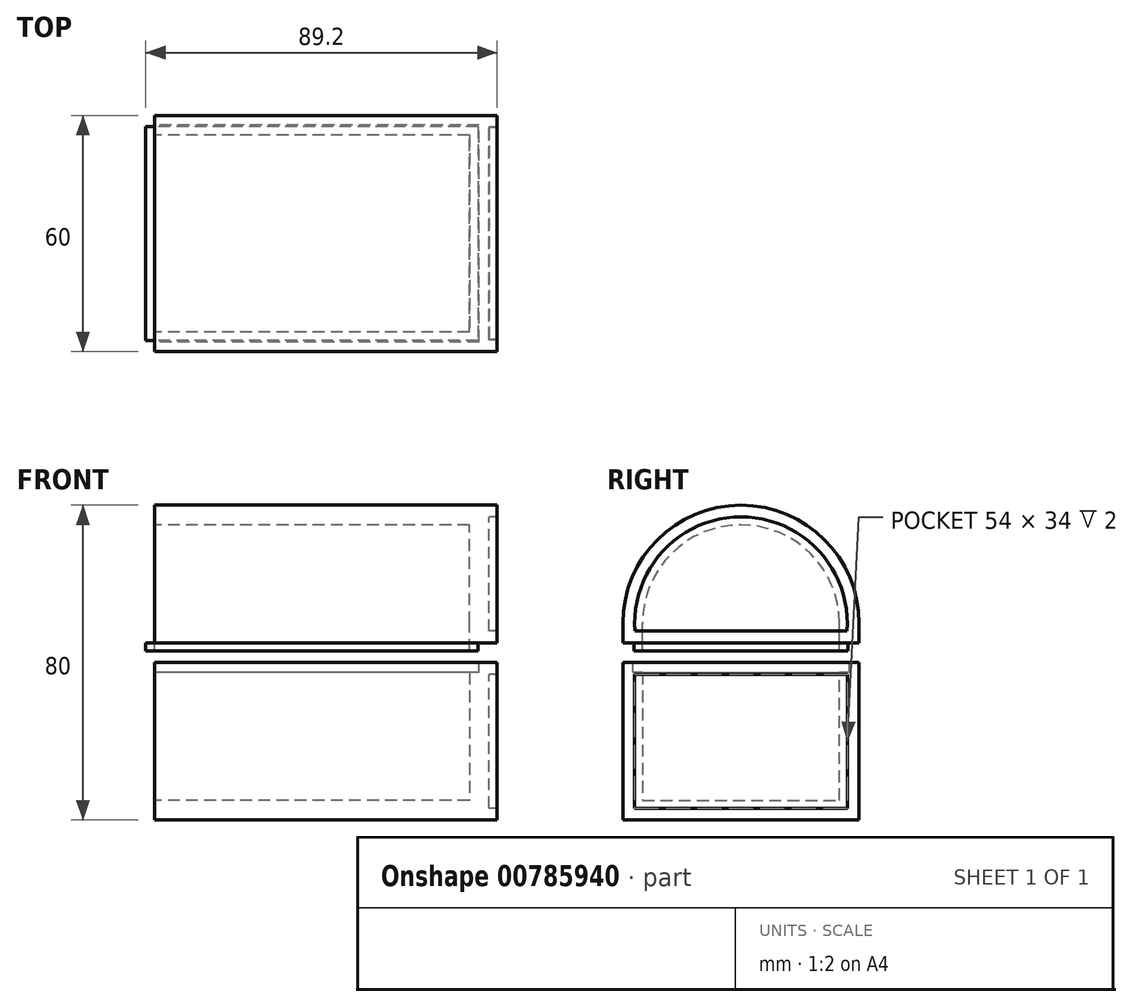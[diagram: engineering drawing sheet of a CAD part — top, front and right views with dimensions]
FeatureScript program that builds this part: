
annotation { "Feature Type Name" : "Feature", "Feature Type Description" : "" }
export const myFeature = defineFeature(function(context is Context, id is Id, definition is map)
    precondition{}
    {
        {
            var Q0;
            Q0=qCreatedBy(makeId("Right.planeOp"),FACE);
            var sketch = newSketch(context, id + "F0", { "sketchPlane" : qUnion([Q0])});
            skLineSegment(sketch, "E0.left", {"start": v(-30, 0) * mm, "end": v(-30, -40) * mm});
            skLineSegment(sketch, "E1.bottom", {"start": v(-30, -40) * mm, "end": v(30, -40) * mm});
            skLineSegment(sketch, "E2.left", {"start": v(30, -40) * mm, "end": v(30, 0) * mm});
            skLineSegment(sketch, "E3.0", {"start": v(25, -35) * mm, "end": v(25, 0) * mm});
            skLineSegment(sketch, "E3.1", {"start": v(-25, -35) * mm, "end": v(25, -35) * mm});
            skLineSegment(sketch, "E3.2", {"start": v(-25, 0) * mm, "end": v(-25, -35) * mm});
            skLineSegment(sketch, "E4", {"start": v(-25, 0) * mm, "end": v(-30, 0) * mm});
            skLineSegment(sketch, "E5", {"start": v(30, 0) * mm, "end": v(25, 0) * mm});
            skSolve(sketch);
        }
        {
            var Q0;
            Q0 = qSketchRegion(id + "F0", true);
            extrude(context, id + "F1", {"entities" : qUnion([Q0]), "endBound" : BoundingType.SYMMETRIC, "depth" : 80 * mm, "offsetDistance" : 25 * mm});
        }
        {
            var Q0;
            Q0=makeQuery(id+"F1.opExtrude","CAP_FACE",FACE,{"disambiguationData":[OSD([sQuery(id+"F0.wireOp",EDGE,"E0.left"),sQuery(id+"F0.wireOp",EDGE,"E1.bottom"),sQuery(id+"F0.wireOp",EDGE,"E2.left"),sQuery(id+"F0.wireOp",EDGE,"E3.0"),sQuery(id+"F0.wireOp",EDGE,"E3.1"),sQuery(id+"F0.wireOp",EDGE,"E3.2"),sQuery(id+"F0.wireOp",EDGE,"E4"),sQuery(id+"F0.wireOp",EDGE,"E5")])],"isStart":false});
            var sketch = newSketch(context, id + "F2", { "sketchPlane" : qUnion([Q0])});
            skLineSegment(sketch, "E6.bottom", {"start": v(-30, 0) * mm, "end": v(30, 0) * mm});
            skLineSegment(sketch, "E6.top", {"start": v(-30, -40) * mm, "end": v(30, -40) * mm});
            skLineSegment(sketch, "E6.left", {"start": v(-30, 0) * mm, "end": v(-30, -40) * mm});
            skLineSegment(sketch, "E6.right", {"start": v(30, 0) * mm, "end": v(30, -40) * mm});
            skSolve(sketch);
        }
        {
            var Q0;
            Q0 = qSketchRegion(id + "F2", true);
            extrude(context, id + "F3", {"entities" : qUnion([Q0]), "operationType" : NewBodyOperationType.ADD, "depth" : 5 * mm, "offsetDistance" : 25 * mm});
        }
        {
            var Q0;
            Q0=makeQuery(id+"F6EYYDIKWfOxyM3_1.boolean.opBoolean","MERGE",FACE,{"derivedFrom":[makeQuery(id+"F3.boolean.opBoolean","MERGE",FACE,{"derivedFrom":[makeQuery(id+"F1.opExtrude","SWEPT_FACE",FACE,{"disambiguationData":[OSD([sQuery(id+"F0.wireOp",EDGE,"E4")])]}),makeQuery(id+"F1.opExtrude","SWEPT_FACE",FACE,{"disambiguationData":[OSD([sQuery(id+"F0.wireOp",EDGE,"E5")])]}),makeQuery(id+"F3.opExtrude","SWEPT_FACE",FACE,{"disambiguationData":[OSD([sQuery(id+"F2.wireOp",EDGE,"E6.bottom")])]})]}),makeQuery(id+"F6EYYDIKWfOxyM3_1.opExtrude","SWEPT_FACE",FACE,{"disambiguationData":[OSD([sQuery(id+"FPHd44v9Huq2bwW_1.wireOp",EDGE,"AvJGf5aJ-Tb4b-4m7N-2CrS-YhxYk3OROw7q.bottom")])]})]});
            var sketch = newSketch(context, id + "F4", { "sketchPlane" : qUnion([Q0])});
            skLineSegment(sketch, "E7.0", {"start": v(40, -25) * mm, "end": v(40, 25) * mm});
            skLineSegment(sketch, "E8.0", {"start": v(40, -25) * mm, "end": v(-40, -25) * mm});
            skLineSegment(sketch, "E9.0", {"start": v(40, 25) * mm, "end": v(-40, 25) * mm});
            skLineSegment(sketch, "E10.0", {"start": v(-40, 25) * mm, "end": v(-40, -25) * mm});
            skLineSegment(sketch, "E11.0", {"start": v(42.5, -27.5) * mm, "end": v(42.5, 27.5) * mm});
            skLineSegment(sketch, "E11.1", {"start": v(42.5, -27.5) * mm, "end": v(-42.5, -27.5) * mm});
            skLineSegment(sketch, "E11.2", {"start": v(-42.5, 27.5) * mm, "end": v(-42.5, -27.5) * mm});
            skLineSegment(sketch, "E11.3", {"start": v(42.5, 27.5) * mm, "end": v(-42.5, 27.5) * mm});
            skSolve(sketch);
        }
        {
            var Q0;
            Q0 = qSketchRegion(id + "F4", true);
            extrude(context, id + "F5", {"entities" : qUnion([Q0]), "operationType" : NewBodyOperationType.REMOVE, "oppositeDirection" : true, "depth" : 2.5 * mm, "offsetDistance" : 25 * mm});
        }
        {
            var Q0;
            Q0=makeQuery(id+"F6EYYDIKWfOxyM3_1.boolean.opBoolean","MERGE",FACE,{"derivedFrom":[makeQuery(id+"F3.boolean.opBoolean","MERGE",FACE,{"derivedFrom":[makeQuery(id+"F1.opExtrude","SWEPT_FACE",FACE,{"disambiguationData":[OSD([sQuery(id+"F0.wireOp",EDGE,"E4")])]}),makeQuery(id+"F1.opExtrude","SWEPT_FACE",FACE,{"disambiguationData":[OSD([sQuery(id+"F0.wireOp",EDGE,"E5")])]}),makeQuery(id+"F3.opExtrude","SWEPT_FACE",FACE,{"disambiguationData":[OSD([sQuery(id+"F2.wireOp",EDGE,"E6.bottom")])]})]}),makeQuery(id+"F6EYYDIKWfOxyM3_1.opExtrude","SWEPT_FACE",FACE,{"disambiguationData":[OSD([sQuery(id+"FPHd44v9Huq2bwW_1.wireOp",EDGE,"AvJGf5aJ-Tb4b-4m7N-2CrS-YhxYk3OROw7q.bottom")])]})]});
            cPlane(context, id + "F6", {"entities" : qUnion([Q0]), "cplaneType" : CPlaneType.OFFSET, "offset" : 5 * mm, "width" : 150 * mm, "height" : 150 * mm});
        }
        {
            var Q0;
            Q0=qCreatedBy(makeId("Right.planeOp"),FACE);
            var sketch = newSketch(context, id + "F7", { "sketchPlane" : qUnion([Q0])});
            skLineSegment(sketch, "E12", {"start": v(-30, 5) * mm, "end": v(-30, 10) * mm});
            skLineSegment(sketch, "E13", {"start": v(30, 5) * mm, "end": v(30, 10) * mm});
            skArc(sketch, "E14", {"start": v(30, 10) * mm, "mid": v(0, 40) * mm, "end": v(-30, 10) * mm});
            skLineSegment(sketch, "E15.0", {"start": v(25, 5) * mm, "end": v(25, 10) * mm});
            skArc(sketch, "E15.1", {"start": v(25, 10) * mm, "mid": v(0, 35) * mm, "end": v(-25, 10) * mm});
            skLineSegment(sketch, "E15.2", {"start": v(-25, 5) * mm, "end": v(-25, 10) * mm});
            skLineSegment(sketch, "E16", {"start": v(-30, 5) * mm, "end": v(-25, 5) * mm});
            skLineSegment(sketch, "E17", {"start": v(30, 5) * mm, "end": v(25, 5) * mm});
            skSolve(sketch);
        }
        {
            var Q0;
            Q0 = qSketchRegion(id + "F7", true);
            extrude(context, id + "F8", {"entities" : qUnion([Q0]), "endBound" : BoundingType.SYMMETRIC, "depth" : 80 * mm, "offsetDistance" : 25 * mm});
        }
        {
            var Q0;
            Q0=makeQuery(id+"F8.opExtrude","CAP_FACE",FACE,{"disambiguationData":[OSD([sQuery(id+"F7.wireOp",EDGE,"E12"),sQuery(id+"F7.wireOp",EDGE,"E13"),sQuery(id+"F7.wireOp",EDGE,"E14"),sQuery(id+"F7.wireOp",EDGE,"E15.0"),sQuery(id+"F7.wireOp",EDGE,"E15.1"),sQuery(id+"F7.wireOp",EDGE,"E15.2"),sQuery(id+"F7.wireOp",EDGE,"E16"),sQuery(id+"F7.wireOp",EDGE,"E17")])],"isStart":false});
            var sketch = newSketch(context, id + "F9", { "sketchPlane" : qUnion([Q0])});
            skArc(sketch, "E18.0", {"start": v(30, 10) * mm, "mid": v(0, 40) * mm, "end": v(-30, 10) * mm});
            skLineSegment(sketch, "E19.0", {"start": v(-30, 5) * mm, "end": v(-30, 10) * mm});
            skLineSegment(sketch, "E20.0", {"start": v(30, 5) * mm, "end": v(30, 10) * mm});
            skLineSegment(sketch, "E21", {"start": v(-30, 5) * mm, "end": v(30, 5) * mm});
            skSolve(sketch);
        }
        {
            var Q0;
            Q0 = qSketchRegion(id + "F9", true);
            extrude(context, id + "F10", {"entities" : qUnion([Q0]), "operationType" : NewBodyOperationType.ADD, "depth" : 5 * mm, "offsetDistance" : 25 * mm});
        }
        {
            var Q0;
            {var subQ0=sQuery(id+"F9.wireOp",EDGE,"E21");Q0=makeQuery(id+"FFZjNm2Aa1Fzhp1_2.1.F10.boolean.opBoolean","MERGE",FACE,{"derivedFrom":[makeQuery(id+"F10.boolean.opBoolean","MERGE",FACE,{"derivedFrom":[makeQuery(id+"F8.opExtrude","SWEPT_FACE",FACE,{"disambiguationData":[OSD([sQuery(id+"F7.wireOp",EDGE,"E16")])]}),makeQuery(id+"F8.opExtrude","SWEPT_FACE",FACE,{"disambiguationData":[OSD([sQuery(id+"F7.wireOp",EDGE,"E17")])]}),makeQuery(id+"F10.opExtrude","SWEPT_FACE",FACE,{"disambiguationData":[OSD([subQ0])]})]}),makeQuery(id+"FFZjNm2Aa1Fzhp1_2.1.F10.opExtrude","SWEPT_FACE",FACE,{"disambiguationData":[OSD([subQ0])]})]});}
            var sketch = newSketch(context, id + "F11", { "sketchPlane" : qUnion([Q0])});
            skLineSegment(sketch, "E22.0", {"start": v(40, 25) * mm, "end": v(-40, 25) * mm});
            skLineSegment(sketch, "E23.0", {"start": v(-40, -25) * mm, "end": v(-40, 25) * mm});
            skLineSegment(sketch, "E24.0", {"start": v(40, -25) * mm, "end": v(-40, -25) * mm});
            skLineSegment(sketch, "E25.0", {"start": v(40, -25) * mm, "end": v(40, 25) * mm});
            skLineSegment(sketch, "E26.0", {"start": v(42.2, 27.2) * mm, "end": v(-42.2, 27.2) * mm});
            skLineSegment(sketch, "E26.1", {"start": v(42.2, -27.2) * mm, "end": v(42.2, 27.2) * mm});
            skLineSegment(sketch, "E26.2", {"start": v(42.2, -27.2) * mm, "end": v(-42.2, -27.2) * mm});
            skLineSegment(sketch, "E26.3", {"start": v(-42.2, -27.2) * mm, "end": v(-42.2, 27.2) * mm});
            skSolve(sketch);
        }
        {
            var Q0;
            Q0 = qSketchRegion(id + "F11", true);
            extrude(context, id + "F12", {"entities" : qUnion([Q0]), "operationType" : NewBodyOperationType.ADD, "depth" : 2 * mm, "offsetDistance" : 25 * mm});
        }
        {
            var Q0;
            Q0=makeQuery(id+"F10.opExtrude","CAP_FACE",FACE,{"disambiguationData":[OSD([sQuery(id+"F9.wireOp",EDGE,"E18.0"),sQuery(id+"F9.wireOp",EDGE,"E19.0"),sQuery(id+"F9.wireOp",EDGE,"E20.0"),sQuery(id+"F9.wireOp",EDGE,"E21")])],"isStart":false});
            var sketch = newSketch(context, id + "F13", { "sketchPlane" : qUnion([Q0])});
            skLineSegment(sketch, "E27.0.0", {"start": v(-30, 10) * mm, "end": v(-30, 5) * mm});
            skLineSegment(sketch, "E27.0.1", {"start": v(-30, 5) * mm, "end": v(30, 5) * mm});
            skLineSegment(sketch, "E27.0.2", {"start": v(30, 5) * mm, "end": v(30, 10) * mm});
            skArc(sketch, "E27.0.3", {"start": v(30, 10) * mm, "mid": v(0, 40) * mm, "end": v(-30, 10) * mm});
            skArc(sketch, "E28.0", {"start": v(26.93, 8) * mm, "mid": v(0, 37) * mm, "end": v(-26.93, 8) * mm});
            skLineSegment(sketch, "E28.1", {"start": v(-26.93, 8) * mm, "end": v(26.93, 8) * mm});
            skSolve(sketch);
        }
        {
            var Q0;
            Q0 = qSketchRegion(id + "F13", true);
            extrude(context, id + "F14", {"entities" : qUnion([Q0]), "operationType" : NewBodyOperationType.ADD, "depth" : 2 * mm, "offsetDistance" : 25 * mm});
        }
        {
            var Q0;
            Q0=makeQuery(id+"F3.opExtrude","CAP_FACE",FACE,{"disambiguationData":[OSD([sQuery(id+"F2.wireOp",EDGE,"E6.bottom"),sQuery(id+"F2.wireOp",EDGE,"E6.top"),sQuery(id+"F2.wireOp",EDGE,"E6.left"),sQuery(id+"F2.wireOp",EDGE,"E6.right")])],"isStart":false});
            var sketch = newSketch(context, id + "F15", { "sketchPlane" : qUnion([Q0])});
            skLineSegment(sketch, "E29.0.0", {"start": v(30, 0) * mm, "end": v(-30, 0) * mm});
            skLineSegment(sketch, "E29.0.1", {"start": v(-30, 0) * mm, "end": v(-30, -40) * mm});
            skLineSegment(sketch, "E29.0.2", {"start": v(-30, -40) * mm, "end": v(30, -40) * mm});
            skLineSegment(sketch, "E29.0.3", {"start": v(30, -40) * mm, "end": v(30, 0) * mm});
            skLineSegment(sketch, "E30.0", {"start": v(27, -3) * mm, "end": v(-27, -3) * mm});
            skLineSegment(sketch, "E30.1", {"start": v(27, -37) * mm, "end": v(27, -3) * mm});
            skLineSegment(sketch, "E30.2", {"start": v(-27, -37) * mm, "end": v(27, -37) * mm});
            skLineSegment(sketch, "E30.3", {"start": v(-27, -3) * mm, "end": v(-27, -37) * mm});
            skSolve(sketch);
        }
        {
            var Q0;
            Q0 = qSketchRegion(id + "F15", true);
            extrude(context, id + "F16", {"entities" : qUnion([Q0]), "operationType" : NewBodyOperationType.ADD, "depth" : 2 * mm, "offsetDistance" : 25 * mm});
        }
    });
